# Revit family: TINO-xxFWSxxxSFx
name_source: partatom
category: Oprawy oświetleniowe
units: mm (PartAtom-declared; Revit-internal decimal feet)

## family parameters
Numer OmniClass = 23.80.70.11
Obiekt nadrzędny = Powierzchnia
Punkt obliczania pomieszczeń = Nie
Tnij formami wycięć po wczytaniu = Nie
Typ części = Normalny
Tytuł OmniClass = Luminaries for Internal Lighting
Współdzielony = Nie
Wymiar okrągłego złącza = Użyj średnicy
Źródło światła = Tak

## types (6) — shared parameters
Emituj kształt widoczny w renderingu = Nie
Emituj ze średnicy okręgu = 65 mm  [stored 0.213255 ft]
Filtr koloru = 16777215
Kod zespołu = D5020200
Lampa = LED
Obciążenie pozorne = 27 VA
Odchylenie kierunku = 90.00°
Plik sieci fotometrycznej = TINO DAFWS840SF0300.IES
Producent = RIDI Leuchten GmbH
URL = www.ridi.de
Zmiana temperatury barwowej przyciemniania lampy = <Brak>
brand = RIDI
conformity mark = CE
electrical safety class = 1
height = 195 mm  [stored 0.639764 ft]
ingress protection (IP) code = IP20
length = 265 mm  [stored 0.869423 ft]
nominal frequency = 50-60Hz
nominal voltage = 230
rated input power = 27
voltage type (AC, DC, UC) = AC
weight = 0,89 kg
width = 92 mm  [stored 0.301837 ft]
zero-valued in all types: Domyślna rzędna

## per-type parameters (varying)
| type | Model |
| TINO NDFWS830SF0300 | 0326737AH |
| TINO DAFWS830SF0300 | 0336737AH |
| TINO NDFWS840SF0300 | 0326741AH |
| TINO DAFWS840SF0300 | 0336741AH |
| TINO NDFWS930SF0250 | 0326745AH |
| TINO DAFWS930SF0250 | 0336745AH |

note: column(s) folded — value = type name in every type: product name

note: [stored X ft] marks values corroborated as IEEE doubles in the binary element streams (Revit-internal decimal feet)
